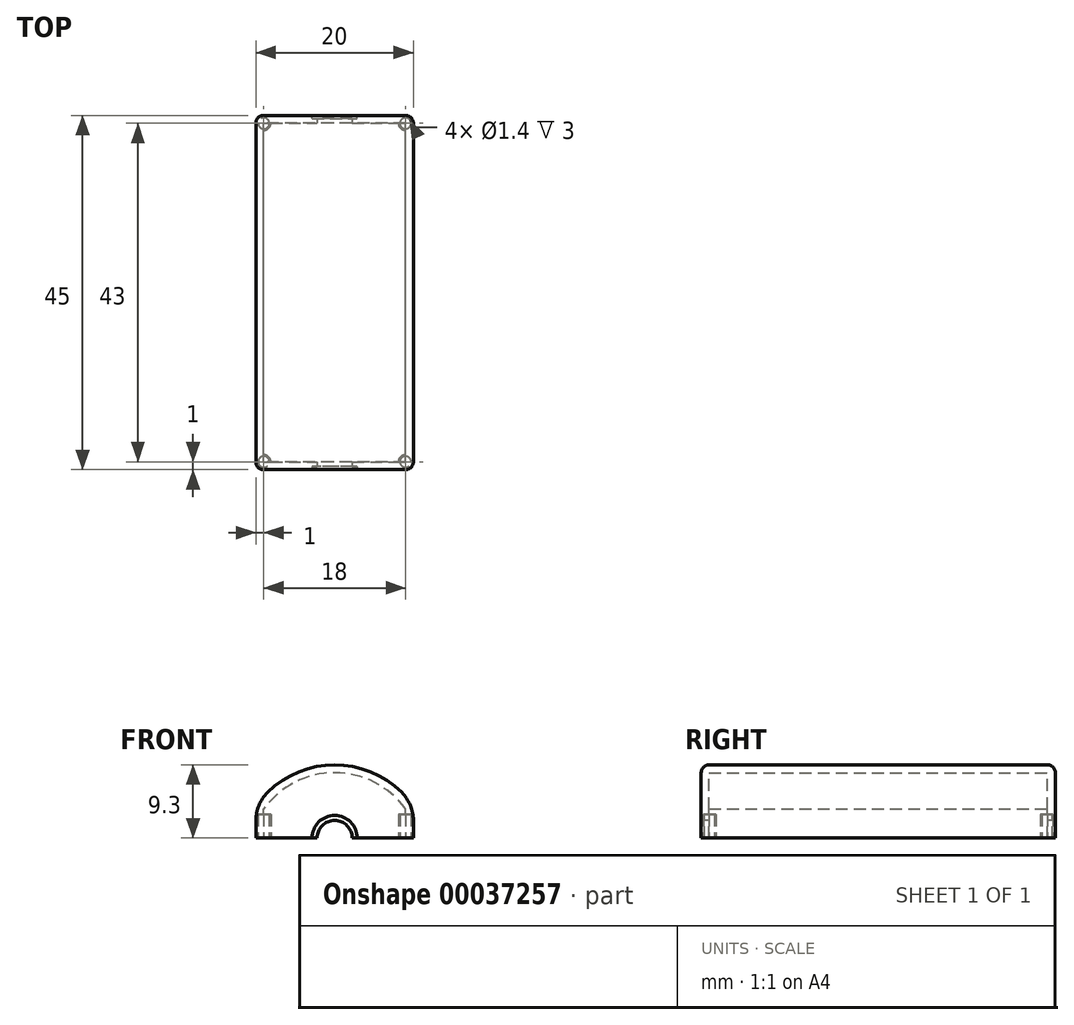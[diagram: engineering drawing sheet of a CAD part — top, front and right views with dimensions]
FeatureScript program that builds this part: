
annotation { "Feature Type Name" : "Feature", "Feature Type Description" : "" }
export const myFeature = defineFeature(function(context is Context, id is Id, definition is map)
    precondition{}
    {
        {
            var Q0;
            Q0=qCreatedBy(makeId("Front.planeOp"),FACE);
            var sketch = newSketch(context, id + "F0", { "sketchPlane" : qUnion([Q0])});
            skLineSegment(sketch, "E0.bottom", {"start": v(0, 0) * mm, "end": v(20, 0) * mm});
            skLineSegment(sketch, "E0.top", {"start": v(0, 4) * mm, "end": v(20, 4) * mm});
            skLineSegment(sketch, "E0.left", {"start": v(0, 0) * mm, "end": v(0, 4) * mm});
            skLineSegment(sketch, "E0.right", {"start": v(20, 0) * mm, "end": v(20, 4) * mm});
            skArc(sketch, "E1", {"start": v(20, 4) * mm, "mid": v(10, 9.3) * mm, "end": v(0, 4) * mm});
            skSolve(sketch);
        }
        {
            var Q0;
            Q0=makeQuery(id+"F0.imprint","IMPRINT",FACE,{"disambiguationData":[TD([[makeQuery(id+"F0.imprint","IMPRINT",EDGE,{"derivedFrom":sQuery(id+"F0.wireOp",EDGE,"E0.bottom")}),1.0]])]});
            var Q1;
            Q1=makeQuery(id+"F0.imprint","IMPRINT",FACE,{"disambiguationData":[TD([[makeQuery(id+"F0.imprint","IMPRINT",EDGE,{"derivedFrom":sQuery(id+"F0.wireOp",EDGE,"E0.top")}),1.0]])]});
            extrude(context, id + "F1", {"entities" : qUnion([Q0, Q1]), "depth" : 45 * mm});
        }
        {
            var Q0;
            Q0=makeQuery(id+"F1.opExtrude","SWEPT_FACE",FACE,{"disambiguationData":[OSD([sQuery(id+"F0.wireOp",EDGE,"E0.bottom")])]});
            shell(context, id + "F2", {"entities" : qUnion([Q0]), "thickness" : 1 * mm});
        }
        {
            var Q0;
            Q0=makeQuery(id+"F1.opExtrude","SWEPT_EDGE",EDGE,{"disambiguationData":[OSD([sQuery(id+"F0.wireOp",EDGE,"E0.top"),sQuery(id+"F0.wireOp",EDGE,"E0.left"),sQuery(id+"F0.wireOp",EDGE,"E1")])]});
            fillet(context, id + "F3", {"entities" : qUnion([Q0]), "radius" : 5 * mm, "tangentPropagation" : true, "allowEdgeOverflow" : false});
        }
        {
            var Q0;
            Q0=makeQuery(id+"F1.opExtrude","SWEPT_EDGE",EDGE,{"disambiguationData":[OSD([sQuery(id+"F0.wireOp",EDGE,"E0.top"),sQuery(id+"F0.wireOp",EDGE,"E0.right"),sQuery(id+"F0.wireOp",EDGE,"E1")])]});
            fillet(context, id + "F4", {"entities" : qUnion([Q0]), "radius" : 5 * mm, "tangentPropagation" : true, "allowEdgeOverflow" : false});
        }
        {
            var Q0;
            Q0=makeQuery(id+"F1.opExtrude","SWEPT_FACE",FACE,{"disambiguationData":[OSD([sQuery(id+"F0.wireOp",EDGE,"E0.bottom")])]});
            var sketch = newSketch(context, id + "F5", { "sketchPlane" : qUnion([Q0])});
            skCircle(sketch, "E2", {"center": v(1, 1) * mm, "radius": 0.9 * mm});
            skCircle(sketch, "E3", {"center": v(19, 1) * mm, "radius": 0.9 * mm});
            skCircle(sketch, "E4", {"center": v(1, 44) * mm, "radius": 0.9 * mm});
            skCircle(sketch, "E5", {"center": v(19, 44) * mm, "radius": 0.9 * mm});
            skSolve(sketch);
        }
        {
            var Q0;
            {var subQ0=sQuery(id+"F0.wireOp",EDGE,"E0.bottom");var subQ1=makeQuery(id+"F2.opShell","OFFSET_EDGE",EDGE,{"disambiguationData":[OSD([subQ0]),TDD([makeQuery(id+"F1.opExtrude","CAP_EDGE",EDGE,{"disambiguationData":[OSD([subQ0])],"isStart":true})])]});var subQ2=sQuery(id+"F5.wireOp",EDGE,"E2");var subQ3=makeQuery(id+"F5.imprint","INTERSECT",VERTEX,{"derivedFrom":[subQ1,subQ2]});Q0=makeQuery(id+"F5.imprint","IMPRINT",FACE,{"disambiguationData":[TD([[makeQuery(id+"F5.imprint","IMPRINT",EDGE,{"disambiguationData":[TD([[subQ3,-1.0]])],"derivedFrom":subQ2}),1.0]])]});}
            var Q1;
            {var subQ0=sQuery(id+"F0.wireOp",EDGE,"E0.bottom");var subQ1=makeQuery(id+"F2.opShell","OFFSET_EDGE",EDGE,{"disambiguationData":[OSD([subQ0]),TDD([makeQuery(id+"F1.opExtrude","CAP_EDGE",EDGE,{"disambiguationData":[OSD([subQ0])],"isStart":true})])]});var subQ2=sQuery(id+"F5.wireOp",EDGE,"E3");var subQ3=makeQuery(id+"F5.imprint","INTERSECT",VERTEX,{"derivedFrom":[subQ1,subQ2]});Q1=makeQuery(id+"F5.imprint","IMPRINT",FACE,{"disambiguationData":[TD([[makeQuery(id+"F5.imprint","IMPRINT",EDGE,{"disambiguationData":[TD([[subQ3,1.0]])],"derivedFrom":subQ2}),1.0]])]});}
            var Q2;
            {var subQ0=sQuery(id+"F0.wireOp",EDGE,"E0.bottom");var subQ1=makeQuery(id+"F2.opShell","OFFSET_EDGE",EDGE,{"disambiguationData":[OSD([subQ0]),TDD([makeQuery(id+"F1.opExtrude","CAP_EDGE",EDGE,{"disambiguationData":[OSD([subQ0])],"isStart":false})])]});var subQ2=sQuery(id+"F5.wireOp",EDGE,"E5");var subQ3=makeQuery(id+"F5.imprint","INTERSECT",VERTEX,{"derivedFrom":[subQ1,subQ2]});Q2=makeQuery(id+"F5.imprint","IMPRINT",FACE,{"disambiguationData":[TD([[makeQuery(id+"F5.imprint","IMPRINT",EDGE,{"disambiguationData":[TD([[subQ3,-1.0]])],"derivedFrom":subQ2}),1.0]])]});}
            var Q3;
            {var subQ0=sQuery(id+"F0.wireOp",EDGE,"E0.bottom");var subQ1=makeQuery(id+"F2.opShell","OFFSET_EDGE",EDGE,{"disambiguationData":[OSD([subQ0]),TDD([makeQuery(id+"F1.opExtrude","CAP_EDGE",EDGE,{"disambiguationData":[OSD([subQ0])],"isStart":false})])]});var subQ2=sQuery(id+"F5.wireOp",EDGE,"E4");var subQ3=makeQuery(id+"F5.imprint","INTERSECT",VERTEX,{"derivedFrom":[subQ1,subQ2]});Q3=makeQuery(id+"F5.imprint","IMPRINT",FACE,{"disambiguationData":[TD([[makeQuery(id+"F5.imprint","IMPRINT",EDGE,{"disambiguationData":[TD([[subQ3,1.0]])],"derivedFrom":subQ2}),1.0]])]});}
            var Q4;
            Q4=sQuery(id+"F5.wireOp",EDGE,"E4");
            var Q5;
            Q5=sQuery(id+"F5.wireOp",EDGE,"E5");
            var Q6;
            Q6=sQuery(id+"F5.wireOp",EDGE,"E2");
            var Q7;
            Q7=sQuery(id+"F5.wireOp",EDGE,"E3");
            extrude(context, id + "F6", {"entities" : qUnion([Q0, Q1, Q2, Q3]), "operationType" : NewBodyOperationType.ADD, "surfaceEntities" : qUnion([Q4, Q5, Q6, Q7]), "oppositeDirection" : true, "depth" : 3 * mm});
        }
        {
            var Q0;
            {var subQ0=sQuery(id+"F0.wireOp",EDGE,"E0.bottom");var subQ1=sQuery(id+"F0.wireOp",EDGE,"E0.left");var subQ2=sQuery(id+"F0.wireOp",EDGE,"E0.right");Q0=makeQuery(id+"F6.boolean.opBoolean","MERGE",FACE,{"derivedFrom":[makeQuery(id+"F1.opExtrude","SWEPT_FACE",FACE,{"disambiguationData":[OSD([subQ0])]}),makeQuery(id+"F6.opExtrude","CAP_FACE",FACE,{"disambiguationData":[OSD([subQ0,subQ1,sQuery(id+"F5.wireOp",EDGE,"E2")])],"isStart":true}),makeQuery(id+"F6.opExtrude","CAP_FACE",FACE,{"disambiguationData":[OSD([subQ0,subQ2,sQuery(id+"F5.wireOp",EDGE,"E3")])],"isStart":true}),makeQuery(id+"F6.opExtrude","CAP_FACE",FACE,{"disambiguationData":[OSD([subQ0,subQ1,sQuery(id+"F5.wireOp",EDGE,"E4")])],"isStart":true}),makeQuery(id+"F6.opExtrude","CAP_FACE",FACE,{"disambiguationData":[OSD([subQ0,subQ2,sQuery(id+"F5.wireOp",EDGE,"E5")])],"isStart":true})]});}
            var sketch = newSketch(context, id + "F7", { "sketchPlane" : qUnion([Q0])});
            skCircle(sketch, "E6", {"center": v(1, 1) * mm, "radius": 0.7 * mm});
            skCircle(sketch, "E7", {"center": v(19, 1) * mm, "radius": 0.7 * mm});
            skCircle(sketch, "E8", {"center": v(1, 44) * mm, "radius": 0.7 * mm});
            skCircle(sketch, "E9", {"center": v(19, 44) * mm, "radius": 0.7 * mm});
            skSolve(sketch);
        }
        {
            var Q0;
            Q0 = qSketchRegion(id + "F7", true);
            extrude(context, id + "F8", {"entities" : qUnion([Q0]), "operationType" : NewBodyOperationType.REMOVE, "oppositeDirection" : true, "depth" : 3 * mm});
        }
        {
            var Q0;
            Q0=makeQuery(id+"F1.opExtrude","CAP_EDGE",EDGE,{"disambiguationData":[OSD([sQuery(id+"F0.wireOp",EDGE,"E0.right")])],"isStart":false});
            var Q1;
            {var subQ0=sQuery(id+"F0.wireOp",EDGE,"E0.right");var subQ1=sQuery(id+"F0.wireOp",EDGE,"E1");Q1=makeQuery(id+"F4.opFillet","BLEND_EDGE",EDGE,{"blendedFrom":[makeQuery(id+"F1.opExtrude","SWEPT_EDGE",EDGE,{"disambiguationData":[OSD([sQuery(id+"F0.wireOp",EDGE,"E0.top"),subQ0,subQ1])]}),makeQuery(id+"F1.opExtrude","CAP_FACE",FACE,{"disambiguationData":[OSD([sQuery(id+"F0.wireOp",EDGE,"E0.bottom"),sQuery(id+"F0.wireOp",EDGE,"E0.left"),subQ0,subQ1])],"isStart":false})],"blendedInto":[makeQuery(id+"F1.opExtrude","CAP_FACE",FACE,{"disambiguationData":[OSD([sQuery(id+"F0.wireOp",EDGE,"E0.bottom"),sQuery(id+"F0.wireOp",EDGE,"E0.left"),subQ0,subQ1])],"isStart":false})]});}
            var Q2;
            Q2=makeQuery(id+"F1.opExtrude","CAP_EDGE",EDGE,{"disambiguationData":[OSD([sQuery(id+"F0.wireOp",EDGE,"E1")])],"isStart":false});
            var Q3;
            {var subQ0=sQuery(id+"F0.wireOp",EDGE,"E0.left");var subQ1=sQuery(id+"F0.wireOp",EDGE,"E1");Q3=makeQuery(id+"F3.opFillet","BLEND_EDGE",EDGE,{"blendedFrom":[makeQuery(id+"F1.opExtrude","SWEPT_EDGE",EDGE,{"disambiguationData":[OSD([sQuery(id+"F0.wireOp",EDGE,"E0.top"),subQ0,subQ1])]}),makeQuery(id+"F1.opExtrude","CAP_FACE",FACE,{"disambiguationData":[OSD([sQuery(id+"F0.wireOp",EDGE,"E0.bottom"),subQ0,sQuery(id+"F0.wireOp",EDGE,"E0.right"),subQ1])],"isStart":false})],"blendedInto":[makeQuery(id+"F1.opExtrude","CAP_FACE",FACE,{"disambiguationData":[OSD([sQuery(id+"F0.wireOp",EDGE,"E0.bottom"),subQ0,sQuery(id+"F0.wireOp",EDGE,"E0.right"),subQ1])],"isStart":false})]});}
            var Q4;
            Q4=makeQuery(id+"F1.opExtrude","CAP_EDGE",EDGE,{"disambiguationData":[OSD([sQuery(id+"F0.wireOp",EDGE,"E0.left")])],"isStart":false});
            fillet(context, id + "F9", {"entities" : qUnion([Q0, Q1, Q2, Q3, Q4]), "radius" : 1 * mm, "tangentPropagation" : true, "allowEdgeOverflow" : false});
        }
        {
            var Q0;
            Q0=makeQuery(id+"F1.opExtrude","CAP_EDGE",EDGE,{"disambiguationData":[OSD([sQuery(id+"F0.wireOp",EDGE,"E0.left")])],"isStart":true});
            var Q1;
            {var subQ0=sQuery(id+"F0.wireOp",EDGE,"E0.left");var subQ1=sQuery(id+"F0.wireOp",EDGE,"E1");Q1=makeQuery(id+"F3.opFillet","BLEND_EDGE",EDGE,{"blendedFrom":[makeQuery(id+"F1.opExtrude","SWEPT_EDGE",EDGE,{"disambiguationData":[OSD([sQuery(id+"F0.wireOp",EDGE,"E0.top"),subQ0,subQ1])]}),makeQuery(id+"F1.opExtrude","CAP_FACE",FACE,{"disambiguationData":[OSD([sQuery(id+"F0.wireOp",EDGE,"E0.bottom"),subQ0,sQuery(id+"F0.wireOp",EDGE,"E0.right"),subQ1])],"isStart":true})],"blendedInto":[makeQuery(id+"F1.opExtrude","CAP_FACE",FACE,{"disambiguationData":[OSD([sQuery(id+"F0.wireOp",EDGE,"E0.bottom"),subQ0,sQuery(id+"F0.wireOp",EDGE,"E0.right"),subQ1])],"isStart":true})]});}
            var Q2;
            Q2=makeQuery(id+"F1.opExtrude","CAP_EDGE",EDGE,{"disambiguationData":[OSD([sQuery(id+"F0.wireOp",EDGE,"E1")])],"isStart":true});
            var Q3;
            {var subQ0=sQuery(id+"F0.wireOp",EDGE,"E0.right");var subQ1=sQuery(id+"F0.wireOp",EDGE,"E1");Q3=makeQuery(id+"F4.opFillet","BLEND_EDGE",EDGE,{"blendedFrom":[makeQuery(id+"F1.opExtrude","SWEPT_EDGE",EDGE,{"disambiguationData":[OSD([sQuery(id+"F0.wireOp",EDGE,"E0.top"),subQ0,subQ1])]}),makeQuery(id+"F1.opExtrude","CAP_FACE",FACE,{"disambiguationData":[OSD([sQuery(id+"F0.wireOp",EDGE,"E0.bottom"),sQuery(id+"F0.wireOp",EDGE,"E0.left"),subQ0,subQ1])],"isStart":true})],"blendedInto":[makeQuery(id+"F1.opExtrude","CAP_FACE",FACE,{"disambiguationData":[OSD([sQuery(id+"F0.wireOp",EDGE,"E0.bottom"),sQuery(id+"F0.wireOp",EDGE,"E0.left"),subQ0,subQ1])],"isStart":true})]});}
            var Q4;
            Q4=makeQuery(id+"F1.opExtrude","CAP_EDGE",EDGE,{"disambiguationData":[OSD([sQuery(id+"F0.wireOp",EDGE,"E0.right")])],"isStart":true});
            fillet(context, id + "F10", {"entities" : qUnion([Q0, Q1, Q2, Q3, Q4]), "radius" : 1 * mm, "tangentPropagation" : true, "allowEdgeOverflow" : false});
        }
        {
            var Q0;
            Q0=makeQuery(id+"F1.opExtrude","CAP_FACE",FACE,{"disambiguationData":[OSD([sQuery(id+"F0.wireOp",EDGE,"E0.bottom"),sQuery(id+"F0.wireOp",EDGE,"E0.left"),sQuery(id+"F0.wireOp",EDGE,"E0.right"),sQuery(id+"F0.wireOp",EDGE,"E1")])],"isStart":false});
            var sketch = newSketch(context, id + "F11", { "sketchPlane" : qUnion([Q0])});
            skCircle(sketch, "E10", {"center": v(10, 0) * mm, "radius": 2.87 * mm});
            skCircle(sketch, "E11", {"center": v(10, 0) * mm, "radius": 2.23 * mm});
            skSolve(sketch);
        }
        {
            var Q0;
            {var subQ0=makeQuery(id+"F1.opExtrude","CAP_EDGE",EDGE,{"disambiguationData":[OSD([sQuery(id+"F0.wireOp",EDGE,"E0.bottom")])],"isStart":false});var subQ1=sQuery(id+"F11.wireOp",EDGE,"E11");var subQ3=makeQuery(id+"F11.imprint","INTERSECT",VERTEX,{"disambiguationData":[OD(0.0)],"derivedFrom":[subQ0,subQ1]});Q0=makeQuery(id+"F11.imprint","IMPRINT",FACE,{"disambiguationData":[TD([[makeQuery(id+"F11.imprint","IMPRINT",EDGE,{"disambiguationData":[TD([[subQ3,1.0]])],"derivedFrom":subQ1}),1.0]])]});}
            extrude(context, id + "F12", {"entities" : qUnion([Q0]), "operationType" : NewBodyOperationType.REMOVE, "oppositeDirection" : true, "depth" : 50 * mm});
        }
        {
            var Q0;
            {var subQ0=makeQuery(id+"F1.opExtrude","CAP_EDGE",EDGE,{"disambiguationData":[OSD([sQuery(id+"F0.wireOp",EDGE,"E0.bottom")])],"isStart":false});var subQ3=sQuery(id+"F11.wireOp",EDGE,"E10");var subQ4=makeQuery(id+"F11.imprint","INTERSECT",VERTEX,{"disambiguationData":[OD(0.0)],"derivedFrom":[subQ0,subQ3]});Q0=makeQuery(id+"F11.imprint","IMPRINT",FACE,{"disambiguationData":[TD([[makeQuery(id+"F11.imprint","IMPRINT",EDGE,{"disambiguationData":[TD([[subQ4,1.0]])],"derivedFrom":subQ3}),1.0]])]});}
            extrude(context, id + "F13", {"entities" : qUnion([Q0]), "operationType" : NewBodyOperationType.REMOVE, "oppositeDirection" : true, "depth" : 0.4 * mm});
        }
        {
            var Q0;
            Q0=makeQuery(id+"F1.opExtrude","CAP_FACE",FACE,{"disambiguationData":[OSD([sQuery(id+"F0.wireOp",EDGE,"E0.bottom"),sQuery(id+"F0.wireOp",EDGE,"E0.left"),sQuery(id+"F0.wireOp",EDGE,"E0.right"),sQuery(id+"F0.wireOp",EDGE,"E1")])],"isStart":true});
            var sketch = newSketch(context, id + "F14", { "sketchPlane" : qUnion([Q0])});
            skCircle(sketch, "E12", {"center": v(-10, 0) * mm, "radius": 2.87 * mm});
            skCircle(sketch, "E13", {"center": v(-10, 0) * mm, "radius": 2.23 * mm});
            skSolve(sketch);
        }
        {
            var Q0;
            {var subQ14=sQuery(id+"F14.wireOp",EDGE,"E13");Q0=makeQuery(id+"F14.imprint","IMPRINT",FACE,{"disambiguationData":[TD([[makeQuery(id+"F14.imprint","IMPRINT",EDGE,{"disambiguationData":[OD(0.0)],"derivedFrom":subQ14}),1.0]])]});}
            extrude(context, id + "F15", {"entities" : qUnion([Q0]), "operationType" : NewBodyOperationType.REMOVE, "oppositeDirection" : true, "depth" : 0.4 * mm});
        }
        {
            var Q0;
            Q0=qCreatedBy(makeId("Top.planeOp"),FACE);
            var sketch = newSketch(context, id + "F16", { "sketchPlane" : qUnion([Q0])});
            skLineSegment(sketch, "E14.bottom", {"start": v(0, 0) * mm, "end": v(20, 0) * mm});
            skLineSegment(sketch, "E14.top", {"start": v(0, -45) * mm, "end": v(20, -45) * mm});
            skLineSegment(sketch, "E14.left", {"start": v(0, 0) * mm, "end": v(0, -45) * mm});
            skLineSegment(sketch, "E14.right", {"start": v(20, 0) * mm, "end": v(20, -45) * mm});
            skLineSegment(sketch, "E15", {"start": v(10, 0) * mm, "end": v(10, -11.25) * mm});
            skLineSegment(sketch, "E16", {"start": v(20, -22.5) * mm, "end": v(15, -22.5) * mm});
            skLineSegment(sketch, "E17", {"start": v(10, -22.5) * mm, "end": v(5, -22.5) * mm});
            skLineSegment(sketch, "E18", {"start": v(10, -22.5) * mm, "end": v(10, -33.75) * mm});
            skLineSegment(sketch, "E19", {"start": v(10, -11.25) * mm, "end": v(10, -22.5) * mm});
            skLineSegment(sketch, "E20", {"start": v(10, -33.75) * mm, "end": v(10, -45) * mm});
            skLineSegment(sketch, "E21", {"start": v(5, -22.5) * mm, "end": v(0, -22.5) * mm});
            skLineSegment(sketch, "E22", {"start": v(15, -22.5) * mm, "end": v(10, -22.5) * mm});
            skSolve(sketch);
        }
        {
            var Q0;
            Q0=qCreatedBy(makeId("Top.planeOp"),FACE);
            cPlane(context, id + "F17", {"entities" : qUnion([Q0]), "cplaneType" : CPlaneType.OFFSET, "offset" : 9.3 * mm, "width" : 150 * mm, "height" : 150 * mm});
        }
    });
